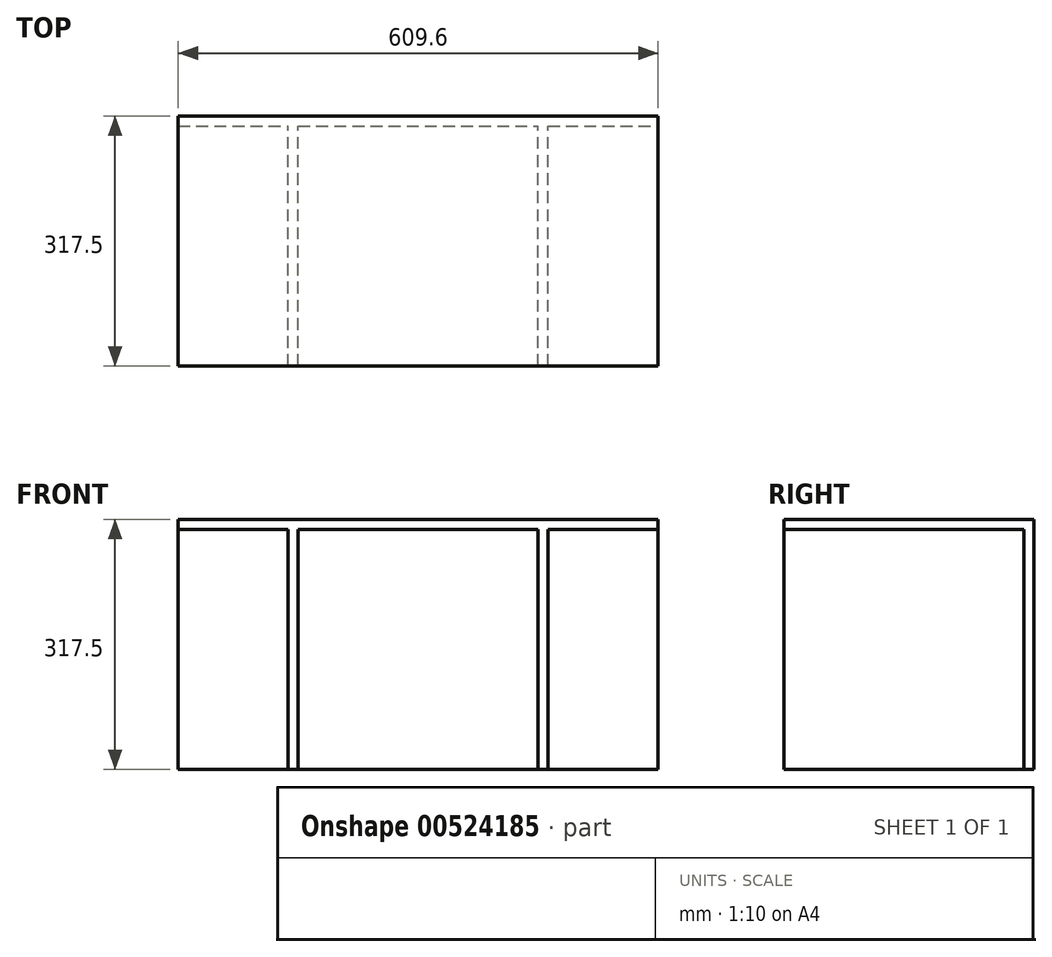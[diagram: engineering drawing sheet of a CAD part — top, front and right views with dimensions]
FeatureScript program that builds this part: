
annotation { "Feature Type Name" : "Feature", "Feature Type Description" : "" }
export const myFeature = defineFeature(function(context is Context, id is Id, definition is map)
    precondition{}
    {
        {
            var Q0;
            Q0=qCreatedBy(makeId("Front.planeOp"),FACE);
            var sketch = newSketch(context, id + "F0", { "sketchPlane" : qUnion([Q0])});
            skLineSegment(sketch, "E0.bottom", {"start": v(-304.8, 0) * mm, "end": v(304.8, 0) * mm});
            skLineSegment(sketch, "E0.top", {"start": v(-304.8, 304.8) * mm, "end": v(304.8, 304.8) * mm});
            skLineSegment(sketch, "E0.left", {"start": v(-304.8, 0) * mm, "end": v(-304.8, 304.8) * mm});
            skLineSegment(sketch, "E0.right", {"start": v(304.8, 0) * mm, "end": v(304.8, 304.8) * mm});
            skLineSegment(sketch, "E1", {"start": v(0, 0) * mm, "end": v(0, 304.8) * mm, "construction": true});
            skSolve(sketch);
        }
        {
            var Q0;
            Q0 = qSketchRegion(id + "F0", true);
            extrude(context, id + "F1", {"entities" : qUnion([Q0]), "depth" : 12.7 * mm, "offsetDistance" : 25.4 * mm});
        }
        {
            var Q0;
            Q0=makeQuery(id+"F1.opExtrude","CAP_FACE",FACE,{"disambiguationData":[OSD([sQuery(id+"F0.wireOp",EDGE,"E0.bottom"),sQuery(id+"F0.wireOp",EDGE,"E0.top"),sQuery(id+"F0.wireOp",EDGE,"E0.left"),sQuery(id+"F0.wireOp",EDGE,"E0.right")])],"isStart":false});
            var sketch = newSketch(context, id + "F2", { "sketchPlane" : qUnion([Q0])});
            skLineSegment(sketch, "E2.bottom", {"start": v(-165.1, 304.8) * mm, "end": v(-152.4, 304.8) * mm});
            skLineSegment(sketch, "E2.top", {"start": v(-165.1, 0) * mm, "end": v(-152.4, 0) * mm});
            skLineSegment(sketch, "E2.left", {"start": v(-165.1, 304.8) * mm, "end": v(-165.1, 0) * mm});
            skLineSegment(sketch, "E2.right", {"start": v(-152.4, 304.8) * mm, "end": v(-152.4, 0) * mm});
            skLineSegment(sketch, "E3.MirrorCS", {"start": v(165.1, 0) * mm, "end": v(152.4, 0) * mm});
            skLineSegment(sketch, "E4.MirrorCS", {"start": v(165.1, 304.8) * mm, "end": v(152.4, 304.8) * mm});
            skLineSegment(sketch, "E5.MirrorCS", {"start": v(152.4, 304.8) * mm, "end": v(152.4, 0) * mm});
            skLineSegment(sketch, "E6.MirrorCS", {"start": v(165.1, 304.8) * mm, "end": v(165.1, 0) * mm});
            skSolve(sketch);
        }
        {
            var Q0;
            Q0 = qSketchRegion(id + "F2", true);
            extrude(context, id + "F3", {"entities" : qUnion([Q0]), "operationType" : NewBodyOperationType.ADD, "depth" : 304.8 * mm, "offsetDistance" : 25.4 * mm});
        }
        {
            var Q0;
            Q0=makeQuery(id+"F3.boolean.opBoolean","MERGE",FACE,{"derivedFrom":[makeQuery(id+"F1.opExtrude","SWEPT_FACE",FACE,{"disambiguationData":[OSD([sQuery(id+"F0.wireOp",EDGE,"E0.top")])]}),makeQuery(id+"F3.opExtrude","SWEPT_FACE",FACE,{"disambiguationData":[OSD([sQuery(id+"F2.wireOp",EDGE,"E2.bottom")])]}),makeQuery(id+"F3.opExtrude","SWEPT_FACE",FACE,{"disambiguationData":[OSD([sQuery(id+"F2.wireOp",EDGE,"E4.MirrorCS")])]})]});
            var sketch = newSketch(context, id + "F4", { "sketchPlane" : qUnion([Q0])});
            skLineSegment(sketch, "E7.bottom", {"start": v(-304.8, 0) * mm, "end": v(304.8, 0) * mm});
            skLineSegment(sketch, "E7.top", {"start": v(-304.8, -317.5) * mm, "end": v(304.8, -317.5) * mm});
            skLineSegment(sketch, "E7.left", {"start": v(-304.8, 0) * mm, "end": v(-304.8, -317.5) * mm});
            skLineSegment(sketch, "E7.right", {"start": v(304.8, 0) * mm, "end": v(304.8, -317.5) * mm});
            skSolve(sketch);
        }
        {
            var Q0;
            Q0 = qSketchRegion(id + "F4", true);
            extrude(context, id + "F5", {"entities" : qUnion([Q0]), "operationType" : NewBodyOperationType.ADD, "depth" : 12.7 * mm, "offsetDistance" : 25.4 * mm});
        }
    });
